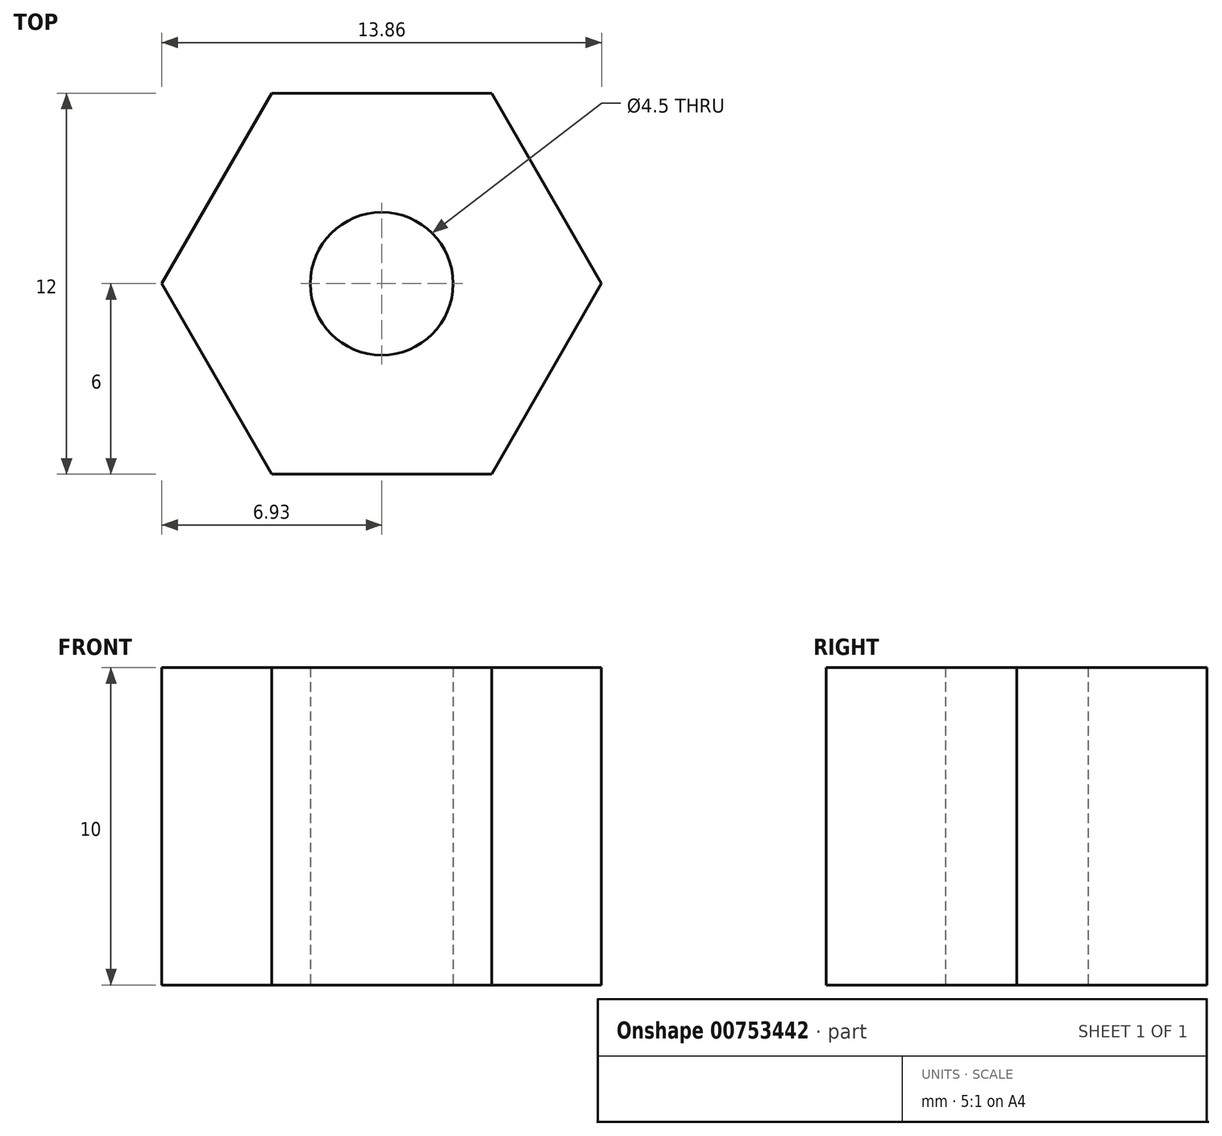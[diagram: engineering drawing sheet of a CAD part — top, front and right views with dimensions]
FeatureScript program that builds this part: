
annotation { "Feature Type Name" : "Feature", "Feature Type Description" : "" }
export const myFeature = defineFeature(function(context is Context, id is Id, definition is map)
    precondition{}
    {
        {
            var Q0;
            Q0=qCreatedBy(makeId("Top.planeOp"),FACE);
            var sketch = newSketch(context, id + "F0", { "sketchPlane" : qUnion([Q0])});
            skCircle(sketch, "E0.cCircle", {"center": v(0, 0) * mm, "radius": 6 * mm, "construction": true});
            skLineSegment(sketch, "E0.0", {"start": v(-3.46, 6) * mm, "end": v(3.46, 6) * mm});
            skLineSegment(sketch, "E0.1", {"start": v(3.46, 6) * mm, "end": v(6.93, 0) * mm});
            skLineSegment(sketch, "E0.2", {"start": v(6.93, 0) * mm, "end": v(3.46, -6) * mm});
            skLineSegment(sketch, "E0.3", {"start": v(3.46, -6) * mm, "end": v(-3.46, -6) * mm});
            skLineSegment(sketch, "E0.4", {"start": v(-3.46, -6) * mm, "end": v(-6.93, 0) * mm});
            skLineSegment(sketch, "E0.5", {"start": v(-6.93, 0) * mm, "end": v(-3.46, 6) * mm});
            skPoint(sketch, "E0.0.midPoint", {"position": v(0, 6) * mm});
            skCircle(sketch, "E1", {"center": v(0, 0) * mm, "radius": 2.25 * mm});
            skSolve(sketch);
        }
        {
            var Q0;
            Q0=makeQuery(id+"F0.imprint","IMPRINT",FACE,{"disambiguationData":[TD([[makeQuery(id+"F0.imprint","IMPRINT",EDGE,{"derivedFrom":sQuery(id+"F0.wireOp",EDGE,"E0.0")}),-1.0]])]});
            extrude(context, id + "F1", {"entities" : qUnion([Q0]), "depth" : 10 * mm, "offsetDistance" : 25 * mm});
        }
    });
